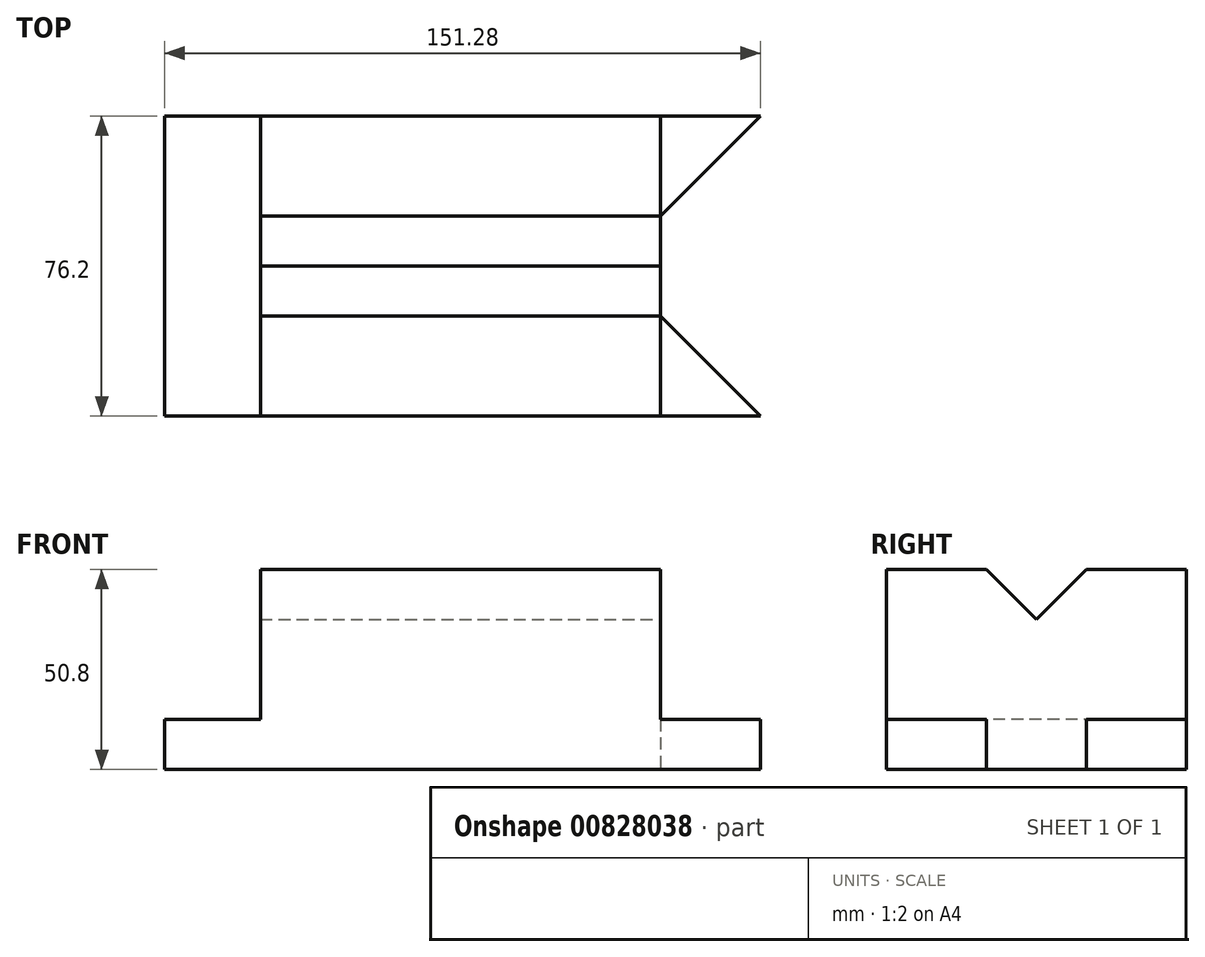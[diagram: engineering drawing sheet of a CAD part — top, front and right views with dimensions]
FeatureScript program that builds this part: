
annotation { "Feature Type Name" : "Feature", "Feature Type Description" : "" }
export const myFeature = defineFeature(function(context is Context, id is Id, definition is map)
    precondition{}
    {
        {
            var Q0;
            Q0=qCreatedBy(makeId("Top.planeOp"),FACE);
            var sketch = newSketch(context, id + "F0", { "sketchPlane" : qUnion([Q0])});
            skLineSegment(sketch, "E0", {"start": v(-45.37, 45.55) * mm, "end": v(56.23, 45.55) * mm});
            skLineSegment(sketch, "E1", {"start": v(56.23, 45.55) * mm, "end": v(56.23, -30.65) * mm});
            skLineSegment(sketch, "E2", {"start": v(56.23, -30.65) * mm, "end": v(-45.37, -30.65) * mm});
            skLineSegment(sketch, "E3", {"start": v(-45.37, -30.65) * mm, "end": v(-45.37, 45.55) * mm});
            skLineSegment(sketch, "E4", {"start": v(-45.37, 45.55) * mm, "end": v(-69.65, 45.55) * mm});
            skLineSegment(sketch, "E5", {"start": v(-69.65, 45.55) * mm, "end": v(-69.65, -30.65) * mm});
            skLineSegment(sketch, "E6", {"start": v(-69.65, -30.65) * mm, "end": v(-45.37, -30.65) * mm});
            skLineSegment(sketch, "E7", {"start": v(56.23, -30.65) * mm, "end": v(81.63, -30.65) * mm});
            skLineSegment(sketch, "E8", {"start": v(81.63, -30.65) * mm, "end": v(56.23, -5.25) * mm});
            skLineSegment(sketch, "E9", {"start": v(56.23, 45.55) * mm, "end": v(81.63, 45.55) * mm});
            skLineSegment(sketch, "E10", {"start": v(81.63, 45.55) * mm, "end": v(56.23, 20.15) * mm});
            skSolve(sketch);
        }
        {
            var Q0;
            Q0=makeQuery(id+"F0.imprint","IMPRINT",FACE,{"disambiguationData":[TD([[makeQuery(id+"F0.imprint","IMPRINT",EDGE,{"derivedFrom":sQuery(id+"F0.wireOp",EDGE,"E3")}),1.0]])]});
            extrude(context, id + "F1", {"entities" : qUnion([Q0]), "depth" : 12.7 * mm, "offsetDistance" : 25.4 * mm});
        }
        {
            var Q0;
            {var subQ4=sQuery(id+"F0.wireOp",EDGE,"E0");Q0=makeQuery(id+"F0.imprint","IMPRINT",FACE,{"disambiguationData":[TD([[makeQuery(id+"F0.imprint","IMPRINT",EDGE,{"derivedFrom":subQ4}),-1.0]])]});}
            extrude(context, id + "F2", {"entities" : qUnion([Q0]), "operationType" : NewBodyOperationType.ADD, "depth" : 50.8 * mm, "offsetDistance" : 25.4 * mm});
        }
        {
            var Q0;
            {var subQ0=sQuery(id+"F0.wireOp",EDGE,"E9");Q0=makeQuery(id+"F0.imprint","IMPRINT",FACE,{"disambiguationData":[TD([[makeQuery(id+"F0.imprint","IMPRINT",EDGE,{"derivedFrom":subQ0}),-1.0]])]});}
            extrude(context, id + "F3", {"entities" : qUnion([Q0]), "operationType" : NewBodyOperationType.ADD, "depth" : 12.7 * mm, "offsetDistance" : 25.4 * mm});
        }
        {
            var Q0;
            {var subQ0=sQuery(id+"F0.wireOp",EDGE,"E7");Q0=makeQuery(id+"F0.imprint","IMPRINT",FACE,{"disambiguationData":[TD([[makeQuery(id+"F0.imprint","IMPRINT",EDGE,{"derivedFrom":subQ0}),1.0]])]});}
            extrude(context, id + "F4", {"entities" : qUnion([Q0]), "operationType" : NewBodyOperationType.ADD, "depth" : 12.7 * mm, "offsetDistance" : 25.4 * mm});
        }
        {
            var Q0;
            Q0=makeQuery(id+"F2.opExtrude","SWEPT_FACE",FACE,{"disambiguationData":[OSD([sQuery(id+"F0.wireOp",EDGE,"E1")])]});
            var sketch = newSketch(context, id + "F5", { "sketchPlane" : qUnion([Q0])});
            skLineSegment(sketch, "E11", {"start": v(-5.25, 50.8) * mm, "end": v(7.45, 38.1) * mm});
            skLineSegment(sketch, "E12", {"start": v(7.45, 38.1) * mm, "end": v(20.15, 50.8) * mm});
            skSolve(sketch);
        }
        {
            var Q0;
            {var subQ0=sQuery(id+"F5.wireOp",EDGE,"E11");Q0=makeQuery(id+"F5.imprint","IMPRINT",FACE,{"disambiguationData":[TD([[makeQuery(id+"F5.imprint","IMPRINT",EDGE,{"derivedFrom":subQ0}),1.0]])]});}
            extrude(context, id + "F6", {"entities" : qUnion([Q0]), "operationType" : NewBodyOperationType.REMOVE, "endBound" : BoundingType.THROUGH_ALL, "oppositeDirection" : true, "depth" : 25.4 * mm, "offsetDistance" : 25.4 * mm});
        }
    });
